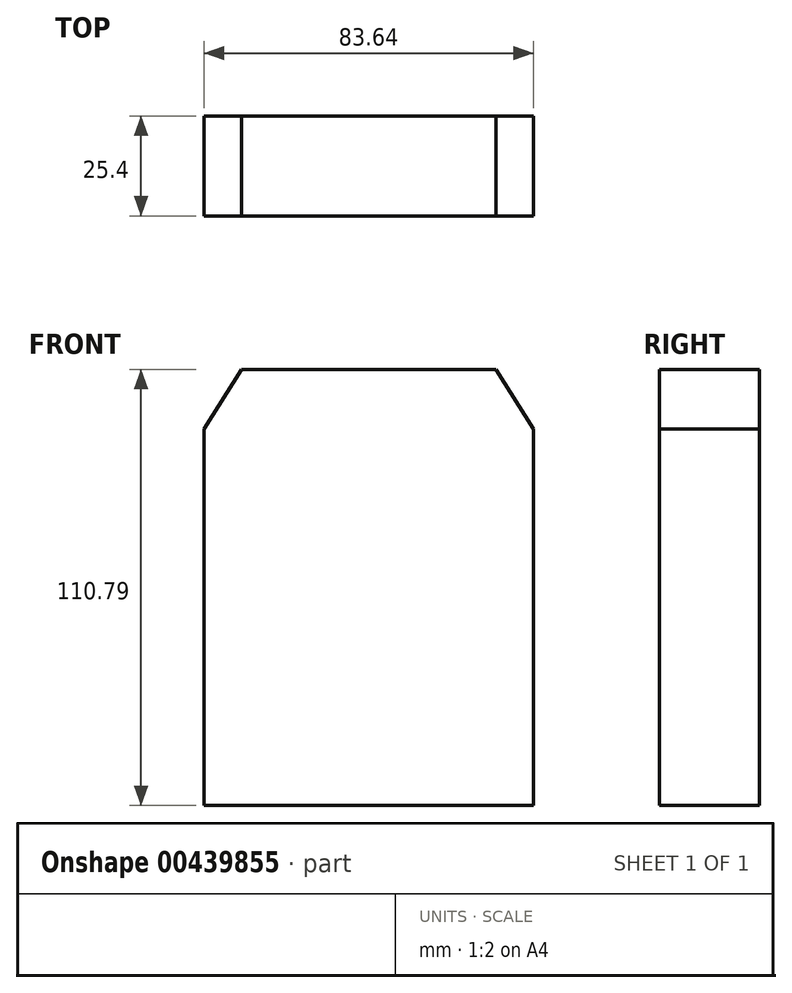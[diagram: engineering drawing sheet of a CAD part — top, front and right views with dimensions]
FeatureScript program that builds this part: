
annotation { "Feature Type Name" : "Feature", "Feature Type Description" : "" }
export const myFeature = defineFeature(function(context is Context, id is Id, definition is map)
    precondition{}
    {
        {
            var Q0;
            Q0=qCreatedBy(makeId("Front.planeOp"),FACE);
            var sketch = newSketch(context, id + "F0", { "sketchPlane" : qUnion([Q0])});
            skLineSegment(sketch, "E0", {"start": v(-32.82, 55.7) * mm, "end": v(31.88, 55.7) * mm});
            skLineSegment(sketch, "E1", {"start": v(31.88, 55.7) * mm, "end": v(41.35, 40.56) * mm});
            skLineSegment(sketch, "E2", {"start": v(-32.82, 55.7) * mm, "end": v(-42.3, 40.56) * mm});
            skLineSegment(sketch, "E3", {"start": v(-42.3, 40.56) * mm, "end": v(-42.3, -55.08) * mm});
            skLineSegment(sketch, "E4", {"start": v(-42.3, -55.08) * mm, "end": v(41.35, -55.08) * mm});
            skLineSegment(sketch, "E5", {"start": v(41.35, -55.08) * mm, "end": v(41.35, 40.56) * mm});
            skSolve(sketch);
        }
        {
            var Q0;
            Q0 = qSketchRegion(id + "F0", true);
            extrude(context, id + "F1", {"entities" : qUnion([Q0]), "depth" : 25.4 * mm});
        }
    });
